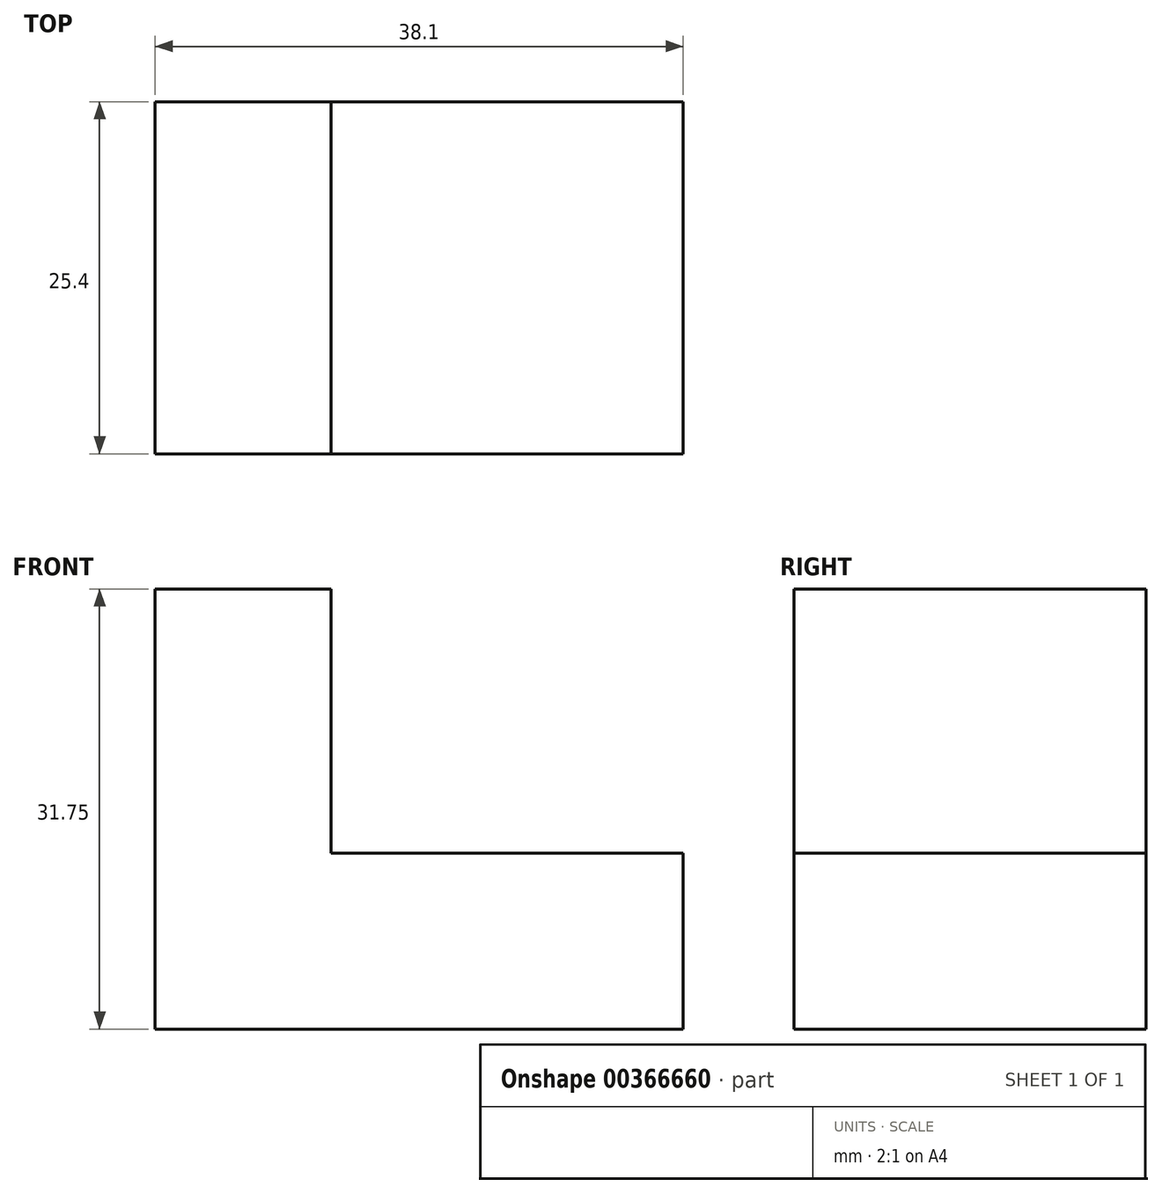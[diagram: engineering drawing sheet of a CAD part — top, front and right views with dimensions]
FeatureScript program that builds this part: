
annotation { "Feature Type Name" : "Feature", "Feature Type Description" : "" }
export const myFeature = defineFeature(function(context is Context, id is Id, definition is map)
    precondition{}
    {
        {
            var Q0;
            Q0=qCreatedBy(makeId("Front.planeOp"),FACE);
            var sketch = newSketch(context, id + "F0", { "sketchPlane" : qUnion([Q0])});
            skLineSegment(sketch, "E0", {"start": v(0, 0) * mm, "end": v(0, 31.75) * mm});
            skLineSegment(sketch, "E1", {"start": v(0, 31.75) * mm, "end": v(12.7, 31.75) * mm});
            skLineSegment(sketch, "E2", {"start": v(0, 0) * mm, "end": v(38.1, 0) * mm});
            skLineSegment(sketch, "E3", {"start": v(12.7, 31.75) * mm, "end": v(12.7, 12.7) * mm});
            skLineSegment(sketch, "E4", {"start": v(12.7, 12.7) * mm, "end": v(38.1, 12.7) * mm});
            skLineSegment(sketch, "E5", {"start": v(38.1, 0) * mm, "end": v(38.1, 12.7) * mm});
            skSolve(sketch);
        }
        {
            var Q0;
            Q0 = qSketchRegion(id + "F0", true);
            extrude(context, id + "F1", {"entities" : qUnion([Q0]), "oppositeDirection" : true, "depth" : 25.4 * mm});
        }
    });
